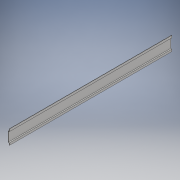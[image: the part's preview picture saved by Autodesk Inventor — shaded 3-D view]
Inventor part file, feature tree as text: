
AUTODESK INVENTOR PART (.ipt)
format: ipt  version: 2018 (Build 220112000, 112)  size: 123,392 bytes
history: native  units: mm
features: extrude x1, sketch x1
ambient origin geometry x8: Origin, YZ Plane, XZ Plane, XY Plane, X Axis, Y Axis, Z Axis, Center Point
bodies: Volumenkörper1 (feature_tree)
feature tree (2):
  extrude  "Extrusion1"  Depth=13.0mm
  sketch  "Skizze1"  dims[d0=1.15mm d1=13.0mm d2=0.3mm d3=0.3mm d4=9.3mm d7=75.0deg d8=0.3mm d9=0.3mm d10=75.0deg d11=0.3mm d12=0.3mm d13=150.0mm d14=0.0mm]
